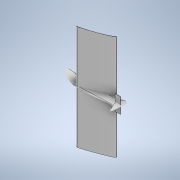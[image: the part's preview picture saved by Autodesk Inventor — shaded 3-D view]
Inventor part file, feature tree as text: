
AUTODESK INVENTOR PART (.ipt)
format: ipt  version: 2022 (Build 260153000, 153)  size: 632,832 bytes
history: native  units: mm
features: other x3, extrude x2, sketch x2, fillet x1
ambient origin geometry x8: Origin, YZ Plane, XZ Plane, XY Plane, X Axis, Y Axis, Z Axis, Center Point
bodies: Body1 (feature_tree), Body2 (feature_tree)
feature tree (8):
  other  "ソリッド1"
  extrude  "押し出し1"  Depth=1.047198mm TaperAngle=0.0deg
  extrude  "押し出し2"  Depth=2.0mm
  fillet  "フィレット6"  Radius=50.0mm
  other  "フォーム2"
  sketch  "スケッチ1"
  sketch  "スケッチ3"
  other  "ソリッド2"
